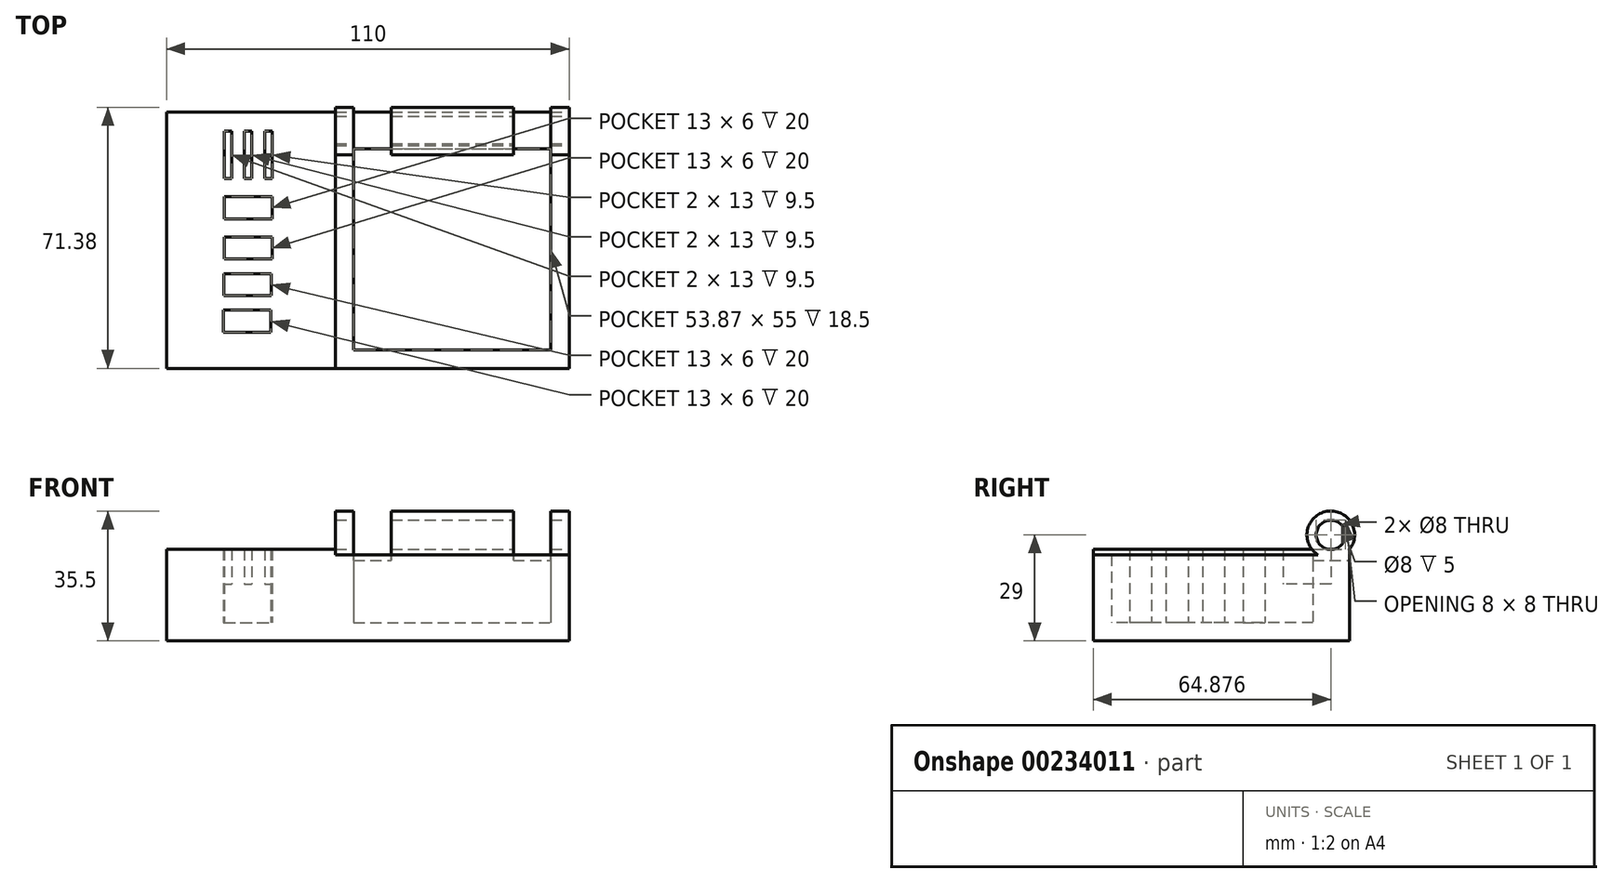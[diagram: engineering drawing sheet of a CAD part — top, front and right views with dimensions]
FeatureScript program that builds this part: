
annotation { "Feature Type Name" : "Feature", "Feature Type Description" : "" }
export const myFeature = defineFeature(function(context is Context, id is Id, definition is map)
    precondition{}
    {
        {
            var Q0;
            Q0=qCreatedBy(makeId("Top.planeOp"),FACE);
            var sketch = newSketch(context, id + "F0", { "sketchPlane" : qUnion([Q0])});
            skLineSegment(sketch, "E0.bottom", {"start": v(0, 0) * mm, "end": v(13, 0) * mm});
            skLineSegment(sketch, "E0.top", {"start": v(0, 6) * mm, "end": v(13, 6) * mm});
            skLineSegment(sketch, "E0.left", {"start": v(0, 0) * mm, "end": v(0, 6) * mm});
            skLineSegment(sketch, "E0.right", {"start": v(13, 0) * mm, "end": v(13, 6) * mm});
            skLineSegment(sketch, "E1.bottom", {"start": v(0, 24) * mm, "end": v(2, 24) * mm});
            skLineSegment(sketch, "E1.top", {"start": v(0, 11) * mm, "end": v(2, 11) * mm});
            skLineSegment(sketch, "E1.left", {"start": v(0, 24) * mm, "end": v(0, 11) * mm});
            skLineSegment(sketch, "E1.right", {"start": v(2, 24) * mm, "end": v(2, 11) * mm});
            skLineSegment(sketch, "E2.bottom", {"start": v(5.5, 24) * mm, "end": v(7.5, 24) * mm});
            skLineSegment(sketch, "E2.top", {"start": v(5.5, 11) * mm, "end": v(7.5, 11) * mm});
            skLineSegment(sketch, "E2.left", {"start": v(5.5, 24) * mm, "end": v(5.5, 11) * mm});
            skLineSegment(sketch, "E2.right", {"start": v(7.5, 24) * mm, "end": v(7.5, 11) * mm});
            skLineSegment(sketch, "E3.bottom", {"start": v(11, 24) * mm, "end": v(13, 24) * mm});
            skLineSegment(sketch, "E3.top", {"start": v(11, 11) * mm, "end": v(13, 11) * mm});
            skLineSegment(sketch, "E3.left", {"start": v(11, 24) * mm, "end": v(11, 11) * mm});
            skLineSegment(sketch, "E3.right", {"start": v(13, 24) * mm, "end": v(13, 11) * mm});
            skLineSegment(sketch, "E4", {"start": v(2, 11) * mm, "end": v(5.5, 11) * mm, "construction": true});
            skLineSegment(sketch, "E5", {"start": v(7.5, 11) * mm, "end": v(11, 11) * mm, "construction": true});
            skLineSegment(sketch, "E6.bottom", {"start": v(0, -5) * mm, "end": v(13, -5) * mm});
            skLineSegment(sketch, "E6.top", {"start": v(0, -11) * mm, "end": v(13, -11) * mm});
            skLineSegment(sketch, "E6.left", {"start": v(0, -5) * mm, "end": v(0, -11) * mm});
            skLineSegment(sketch, "E6.right", {"start": v(13, -5) * mm, "end": v(13, -11) * mm});
            skLineSegment(sketch, "E7.bottom", {"start": v(35.31, 19.1) * mm, "end": v(89.18, 19.1) * mm});
            skLineSegment(sketch, "E7.top", {"start": v(35.32, -35.9) * mm, "end": v(89.19, -35.9) * mm});
            skLineSegment(sketch, "E7.left", {"start": v(35.31, 19.1) * mm, "end": v(35.32, -35.9) * mm});
            skLineSegment(sketch, "E7.right", {"start": v(89.18, 19.1) * mm, "end": v(89.19, -35.9) * mm});
            skLineSegment(sketch, "E8.bottom", {"start": v(-15.81, -40.9) * mm, "end": v(94.19, -40.9) * mm});
            skLineSegment(sketch, "E8.top", {"start": v(-15.82, 29.1) * mm, "end": v(94.19, 29.1) * mm});
            skLineSegment(sketch, "E8.left", {"start": v(-15.81, -40.9) * mm, "end": v(-15.82, 29.1) * mm});
            skLineSegment(sketch, "E8.right", {"start": v(94.19, -40.9) * mm, "end": v(94.19, 29.1) * mm});
            skLineSegment(sketch, "E9.1.0.0", {"start": v(-0.16, -21) * mm, "end": v(12.84, -21) * mm});
            skLineSegment(sketch, "E9.1.0.1", {"start": v(-0.16, -15) * mm, "end": v(-0.16, -21) * mm});
            skLineSegment(sketch, "E9.1.0.2", {"start": v(-0.16, -15) * mm, "end": v(12.84, -15) * mm});
            skLineSegment(sketch, "E9.1.0.3", {"start": v(12.84, -15) * mm, "end": v(12.84, -21) * mm});
            skLineSegment(sketch, "E9.2.0.0", {"start": v(-0.31, -31) * mm, "end": v(12.69, -31) * mm});
            skLineSegment(sketch, "E9.2.0.1", {"start": v(-0.31, -25) * mm, "end": v(-0.31, -31) * mm});
            skLineSegment(sketch, "E9.2.0.2", {"start": v(-0.31, -25) * mm, "end": v(12.69, -25) * mm});
            skLineSegment(sketch, "E9.2.0.3", {"start": v(12.69, -25) * mm, "end": v(12.69, -31) * mm});
            skLineSegment(sketch, "E9.direction1", {"start": v(0, -11) * mm, "end": v(-0.16, -21) * mm, "construction": true});
            skSolve(sketch);
        }
        {
            var Q0;
            Q0=makeQuery(id+"F0.imprint","IMPRINT",FACE,{"disambiguationData":[TD([[makeQuery(id+"F0.imprint","IMPRINT",EDGE,{"derivedFrom":sQuery(id+"F0.wireOp",EDGE,"E0.bottom")}),-1.0]])]});
            extrude(context, id + "F1", {"entities" : qUnion([Q0]), "depth" : 25 * mm});
        }
        {
            var Q0;
            Q0=makeQuery(id+"F1.opExtrude","CAP_FACE",FACE,{"disambiguationData":[OSD([sQuery(id+"F0.wireOp",EDGE,"E0.bottom"),sQuery(id+"F0.wireOp",EDGE,"E0.top"),sQuery(id+"F0.wireOp",EDGE,"E0.left"),sQuery(id+"F0.wireOp",EDGE,"E0.right"),sQuery(id+"F0.wireOp",EDGE,"E1.bottom"),sQuery(id+"F0.wireOp",EDGE,"E1.top"),sQuery(id+"F0.wireOp",EDGE,"E1.left"),sQuery(id+"F0.wireOp",EDGE,"E1.right"),sQuery(id+"F0.wireOp",EDGE,"E2.bottom"),sQuery(id+"F0.wireOp",EDGE,"E2.top"),sQuery(id+"F0.wireOp",EDGE,"E2.left"),sQuery(id+"F0.wireOp",EDGE,"E2.right"),sQuery(id+"F0.wireOp",EDGE,"E3.bottom"),sQuery(id+"F0.wireOp",EDGE,"E3.top"),sQuery(id+"F0.wireOp",EDGE,"E3.left"),sQuery(id+"F0.wireOp",EDGE,"E3.right"),sQuery(id+"F0.wireOp",EDGE,"E6.bottom"),sQuery(id+"F0.wireOp",EDGE,"E6.top"),sQuery(id+"F0.wireOp",EDGE,"E6.left"),sQuery(id+"F0.wireOp",EDGE,"E6.right"),sQuery(id+"F0.wireOp",EDGE,"Jhem5B7e-PwaY-wi88-L2AS-oDyRLYaUdTvM.top"),sQuery(id+"F0.wireOp",EDGE,"Jhem5B7e-PwaY-wi88-L2AS-oDyRLYaUdTvM.right"),sQuery(id+"F0.wireOp",EDGE,"dHCuu3V0-Hv5L-0egd-wwGA-Vg7BnMR16jFB.bottom"),sQuery(id+"F0.wireOp",EDGE,"dHCuu3V0-Hv5L-0egd-wwGA-Vg7BnMR16jFB.top"),sQuery(id+"F0.wireOp",EDGE,"dHCuu3V0-Hv5L-0egd-wwGA-Vg7BnMR16jFB.left"),sQuery(id+"F0.wireOp",EDGE,"dHCuu3V0-Hv5L-0egd-wwGA-Vg7BnMR16jFB.right"),sQuery(id+"F0.wireOp",EDGE,"6ZkocFOk-AnUZ-cton-rGbu-JuxtpcTcdqMe"),sQuery(id+"F0.wireOp",EDGE,"PdukZ5u5-dsJj-gbYv-5oKE-4uIxkKqPsWSn"),sQuery(id+"F0.wireOp",EDGE,"E7.bottom"),sQuery(id+"F0.wireOp",EDGE,"E7.top"),sQuery(id+"F0.wireOp",EDGE,"E7.left"),sQuery(id+"F0.wireOp",EDGE,"E7.right"),sQuery(id+"F0.wireOp",EDGE,"E8.bottom"),sQuery(id+"F0.wireOp",EDGE,"E8.top"),sQuery(id+"F0.wireOp",EDGE,"E8.left"),sQuery(id+"F0.wireOp",EDGE,"E8.right")])],"isStart":true});
            var sketch = newSketch(context, id + "F2", { "sketchPlane" : qUnion([Q0])});
            skLineSegment(sketch, "E10.bottom", {"start": v(89.18, -19.1) * mm, "end": v(35.32, -19.1) * mm});
            skLineSegment(sketch, "E10.top", {"start": v(89.18, 35.9) * mm, "end": v(35.32, 35.9) * mm});
            skLineSegment(sketch, "E10.left", {"start": v(89.18, -19.1) * mm, "end": v(89.18, 35.9) * mm});
            skLineSegment(sketch, "E10.right", {"start": v(35.32, -19.1) * mm, "end": v(35.32, 35.9) * mm});
            skLineSegment(sketch, "E11.bottom", {"start": v(13, -6) * mm, "end": v(0, -6) * mm});
            skLineSegment(sketch, "E11.top", {"start": v(13, 0) * mm, "end": v(0, 0) * mm});
            skLineSegment(sketch, "E11.left", {"start": v(13, -6) * mm, "end": v(13, 0) * mm});
            skLineSegment(sketch, "E11.right", {"start": v(0, -6) * mm, "end": v(0, 0) * mm});
            skLineSegment(sketch, "E12.bottom", {"start": v(13, 5) * mm, "end": v(0, 5) * mm});
            skLineSegment(sketch, "E12.top", {"start": v(13, 11) * mm, "end": v(0, 11) * mm});
            skLineSegment(sketch, "E12.left", {"start": v(13, 5) * mm, "end": v(13, 11) * mm});
            skLineSegment(sketch, "E12.right", {"start": v(0, 5) * mm, "end": v(0, 11) * mm});
            skSolve(sketch);
        }
        {
            var Q0;
            Q0=makeQuery(id+"F2.imprint","IMPRINT",FACE,{"disambiguationData":[TD([[makeQuery(id+"F2.imprint","IMPRINT",EDGE,{"derivedFrom":sQuery(id+"F2.wireOp",EDGE,"E10.bottom")}),1.0]])]});
            var Q1;
            Q1=makeQuery(id+"F2.imprint","IMPRINT",FACE,{"disambiguationData":[TD([[makeQuery(id+"F2.imprint","IMPRINT",EDGE,{"derivedFrom":sQuery(id+"F2.wireOp",EDGE,"E11.bottom")}),1.0]])]});
            var Q2;
            Q2=makeQuery(id+"F2.imprint","IMPRINT",FACE,{"disambiguationData":[TD([[makeQuery(id+"F2.imprint","IMPRINT",EDGE,{"derivedFrom":sQuery(id+"F2.wireOp",EDGE,"E12.bottom")}),1.0]])]});
            var Q3;
            Q3=makeQuery(id+"F2.imprint","IMPRINT",FACE,{"disambiguationData":[TD([[makeQuery(id+"F2.imprint","IMPRINT",EDGE,{"derivedFrom":sQuery(id+"F2.wireOp",EDGE,"BDkRQzdd-od42-jESW-7ooD-0bF7jNIlFtZo.bottom")}),1.0]])]});
            var Q4;
            Q4=makeQuery(id+"F2.imprint","IMPRINT",FACE,{"disambiguationData":[TD([[makeQuery(id+"F2.imprint","IMPRINT",EDGE,{"derivedFrom":sQuery(id+"F2.wireOp",EDGE,"YnWAU6LA-DngU-H7TV-ikAZ-Mie4OEYWa2Z2.bottom")}),1.0]])]});
            extrude(context, id + "F3", {"entities" : qUnion([Q0, Q1, Q2, Q3, Q4]), "operationType" : NewBodyOperationType.ADD, "oppositeDirection" : true, "depth" : 5 * mm});
        }
        {
            var Q0;
            Q0=makeQuery(id+"F3.boolean.opBoolean","MERGE",FACE,{"derivedFrom":[makeQuery(id+"F1.opExtrude","CAP_FACE",FACE,{"disambiguationData":[OSD([sQuery(id+"F0.wireOp",EDGE,"E0.bottom"),sQuery(id+"F0.wireOp",EDGE,"E0.top"),sQuery(id+"F0.wireOp",EDGE,"E0.left"),sQuery(id+"F0.wireOp",EDGE,"E0.right"),sQuery(id+"F0.wireOp",EDGE,"E1.bottom"),sQuery(id+"F0.wireOp",EDGE,"E1.top"),sQuery(id+"F0.wireOp",EDGE,"E1.left"),sQuery(id+"F0.wireOp",EDGE,"E1.right"),sQuery(id+"F0.wireOp",EDGE,"E2.bottom"),sQuery(id+"F0.wireOp",EDGE,"E2.top"),sQuery(id+"F0.wireOp",EDGE,"E2.left"),sQuery(id+"F0.wireOp",EDGE,"E2.right"),sQuery(id+"F0.wireOp",EDGE,"E3.bottom"),sQuery(id+"F0.wireOp",EDGE,"E3.top"),sQuery(id+"F0.wireOp",EDGE,"E3.left"),sQuery(id+"F0.wireOp",EDGE,"E3.right"),sQuery(id+"F0.wireOp",EDGE,"E6.bottom"),sQuery(id+"F0.wireOp",EDGE,"E6.top"),sQuery(id+"F0.wireOp",EDGE,"E6.left"),sQuery(id+"F0.wireOp",EDGE,"E6.right"),sQuery(id+"F0.wireOp",EDGE,"Jhem5B7e-PwaY-wi88-L2AS-oDyRLYaUdTvM.top"),sQuery(id+"F0.wireOp",EDGE,"Jhem5B7e-PwaY-wi88-L2AS-oDyRLYaUdTvM.right"),sQuery(id+"F0.wireOp",EDGE,"dHCuu3V0-Hv5L-0egd-wwGA-Vg7BnMR16jFB.bottom"),sQuery(id+"F0.wireOp",EDGE,"dHCuu3V0-Hv5L-0egd-wwGA-Vg7BnMR16jFB.top"),sQuery(id+"F0.wireOp",EDGE,"dHCuu3V0-Hv5L-0egd-wwGA-Vg7BnMR16jFB.left"),sQuery(id+"F0.wireOp",EDGE,"dHCuu3V0-Hv5L-0egd-wwGA-Vg7BnMR16jFB.right"),sQuery(id+"F0.wireOp",EDGE,"6ZkocFOk-AnUZ-cton-rGbu-JuxtpcTcdqMe"),sQuery(id+"F0.wireOp",EDGE,"PdukZ5u5-dsJj-gbYv-5oKE-4uIxkKqPsWSn"),sQuery(id+"F0.wireOp",EDGE,"E7.bottom"),sQuery(id+"F0.wireOp",EDGE,"E7.top"),sQuery(id+"F0.wireOp",EDGE,"E7.left"),sQuery(id+"F0.wireOp",EDGE,"E7.right"),sQuery(id+"F0.wireOp",EDGE,"E8.bottom"),sQuery(id+"F0.wireOp",EDGE,"E8.top"),sQuery(id+"F0.wireOp",EDGE,"E8.left"),sQuery(id+"F0.wireOp",EDGE,"E8.right")])],"isStart":true}),makeQuery(id+"F3.opExtrude","CAP_FACE",FACE,{"disambiguationData":[OSD([sQuery(id+"F2.wireOp",EDGE,"E10.bottom"),sQuery(id+"F2.wireOp",EDGE,"E10.top"),sQuery(id+"F2.wireOp",EDGE,"E10.left"),sQuery(id+"F2.wireOp",EDGE,"E10.right")])],"isStart":true}),makeQuery(id+"F3.opExtrude","CAP_FACE",FACE,{"disambiguationData":[OSD([sQuery(id+"F2.wireOp",EDGE,"E11.bottom"),sQuery(id+"F2.wireOp",EDGE,"E11.top"),sQuery(id+"F2.wireOp",EDGE,"E11.left"),sQuery(id+"F2.wireOp",EDGE,"E11.right")])],"isStart":true}),makeQuery(id+"F3.opExtrude","CAP_FACE",FACE,{"disambiguationData":[OSD([sQuery(id+"F2.wireOp",EDGE,"E12.bottom"),sQuery(id+"F2.wireOp",EDGE,"E12.top"),sQuery(id+"F2.wireOp",EDGE,"E12.left"),sQuery(id+"F2.wireOp",EDGE,"E12.right")])],"isStart":true}),makeQuery(id+"F3.opExtrude","CAP_FACE",FACE,{"disambiguationData":[OSD([sQuery(id+"F2.wireOp",EDGE,"YnWAU6LA-DngU-H7TV-ikAZ-Mie4OEYWa2Z2.bottom"),sQuery(id+"F2.wireOp",EDGE,"YnWAU6LA-DngU-H7TV-ikAZ-Mie4OEYWa2Z2.top"),sQuery(id+"F2.wireOp",EDGE,"YnWAU6LA-DngU-H7TV-ikAZ-Mie4OEYWa2Z2.left"),sQuery(id+"F2.wireOp",EDGE,"YnWAU6LA-DngU-H7TV-ikAZ-Mie4OEYWa2Z2.right")])],"isStart":true}),makeQuery(id+"F3.opExtrude","CAP_FACE",FACE,{"disambiguationData":[OSD([sQuery(id+"F2.wireOp",EDGE,"BDkRQzdd-od42-jESW-7ooD-0bF7jNIlFtZo.bottom"),sQuery(id+"F2.wireOp",EDGE,"BDkRQzdd-od42-jESW-7ooD-0bF7jNIlFtZo.top"),sQuery(id+"F2.wireOp",EDGE,"BDkRQzdd-od42-jESW-7ooD-0bF7jNIlFtZo.left"),sQuery(id+"F2.wireOp",EDGE,"BDkRQzdd-od42-jESW-7ooD-0bF7jNIlFtZo.right")])],"isStart":true})]});
            var sketch = newSketch(context, id + "F4", { "sketchPlane" : qUnion([Q0])});
            skLineSegment(sketch, "E13.bottom", {"start": v(13, -24) * mm, "end": v(11, -24) * mm});
            skLineSegment(sketch, "E13.top", {"start": v(13, -11) * mm, "end": v(11, -11) * mm});
            skLineSegment(sketch, "E13.left", {"start": v(13, -24) * mm, "end": v(13, -11) * mm});
            skLineSegment(sketch, "E13.right", {"start": v(11, -24) * mm, "end": v(11, -11) * mm});
            skLineSegment(sketch, "E14.bottom", {"start": v(7.5, -11) * mm, "end": v(5.5, -11) * mm});
            skLineSegment(sketch, "E14.top", {"start": v(7.5, -24) * mm, "end": v(5.5, -24) * mm});
            skLineSegment(sketch, "E14.left", {"start": v(7.5, -11) * mm, "end": v(7.5, -24) * mm});
            skLineSegment(sketch, "E14.right", {"start": v(5.5, -11) * mm, "end": v(5.5, -24) * mm});
            skLineSegment(sketch, "E15.bottom", {"start": v(2, -24) * mm, "end": v(0, -24) * mm});
            skLineSegment(sketch, "E15.top", {"start": v(2, -11) * mm, "end": v(0, -11) * mm});
            skLineSegment(sketch, "E15.left", {"start": v(2, -24) * mm, "end": v(2, -11) * mm});
            skLineSegment(sketch, "E15.right", {"start": v(0, -24) * mm, "end": v(0, -11) * mm});
            skSolve(sketch);
        }
        {
            var Q0;
            Q0=makeQuery(id+"F4.imprint","IMPRINT",FACE,{"disambiguationData":[TD([[makeQuery(id+"F4.imprint","IMPRINT",EDGE,{"derivedFrom":sQuery(id+"F4.wireOp",EDGE,"E13.bottom")}),1.0]])]});
            var Q1;
            Q1=makeQuery(id+"F4.imprint","IMPRINT",FACE,{"disambiguationData":[TD([[makeQuery(id+"F4.imprint","IMPRINT",EDGE,{"derivedFrom":sQuery(id+"F4.wireOp",EDGE,"E14.bottom")}),-1.0]])]});
            var Q2;
            Q2=makeQuery(id+"F4.imprint","IMPRINT",FACE,{"disambiguationData":[TD([[makeQuery(id+"F4.imprint","IMPRINT",EDGE,{"derivedFrom":sQuery(id+"F4.wireOp",EDGE,"E15.bottom")}),1.0]])]});
            extrude(context, id + "F5", {"entities" : qUnion([Q0, Q1, Q2]), "operationType" : NewBodyOperationType.ADD, "oppositeDirection" : true, "depth" : (25 - 9.5) * mm});
        }
        {
            var Q0;
            Q0=makeQuery(id+"F1.opExtrude","SWEPT_FACE",FACE,{"disambiguationData":[OSD([sQuery(id+"F0.wireOp",EDGE,"E8.right")])]});
            var sketch = newSketch(context, id + "F6", { "sketchPlane" : qUnion([Q0])});
            skCircle(sketch, "E16", {"center": v(23.98, 29) * mm, "radius": 4 * mm});
            skCircle(sketch, "E17", {"center": v(23.98, 29) * mm, "radius": 6.5 * mm});
            skSolve(sketch);
        }
        {
            var Q0;
            Q0 = qSketchRegion(id + "F6", true);
            extrude(context, id + "F7", {"entities" : qUnion([Q0]), "operationType" : NewBodyOperationType.ADD, "oppositeDirection" : true, "depth" : (53.87 + 10) * mm});
        }
        {
            var Q0;
            Q0=makeQuery(id+"F1.opExtrude","CAP_FACE",FACE,{"disambiguationData":[OSD([sQuery(id+"F0.wireOp",EDGE,"E0.bottom"),sQuery(id+"F0.wireOp",EDGE,"E0.top"),sQuery(id+"F0.wireOp",EDGE,"E0.left"),sQuery(id+"F0.wireOp",EDGE,"E0.right"),sQuery(id+"F0.wireOp",EDGE,"E1.bottom"),sQuery(id+"F0.wireOp",EDGE,"E1.top"),sQuery(id+"F0.wireOp",EDGE,"E1.left"),sQuery(id+"F0.wireOp",EDGE,"E1.right"),sQuery(id+"F0.wireOp",EDGE,"E2.bottom"),sQuery(id+"F0.wireOp",EDGE,"E2.top"),sQuery(id+"F0.wireOp",EDGE,"E2.left"),sQuery(id+"F0.wireOp",EDGE,"E2.right"),sQuery(id+"F0.wireOp",EDGE,"E3.bottom"),sQuery(id+"F0.wireOp",EDGE,"E3.top"),sQuery(id+"F0.wireOp",EDGE,"E3.left"),sQuery(id+"F0.wireOp",EDGE,"E3.right"),sQuery(id+"F0.wireOp",EDGE,"E6.bottom"),sQuery(id+"F0.wireOp",EDGE,"E6.top"),sQuery(id+"F0.wireOp",EDGE,"E6.left"),sQuery(id+"F0.wireOp",EDGE,"E6.right"),sQuery(id+"F0.wireOp",EDGE,"Jhem5B7e-PwaY-wi88-L2AS-oDyRLYaUdTvM.top"),sQuery(id+"F0.wireOp",EDGE,"Jhem5B7e-PwaY-wi88-L2AS-oDyRLYaUdTvM.right"),sQuery(id+"F0.wireOp",EDGE,"dHCuu3V0-Hv5L-0egd-wwGA-Vg7BnMR16jFB.bottom"),sQuery(id+"F0.wireOp",EDGE,"dHCuu3V0-Hv5L-0egd-wwGA-Vg7BnMR16jFB.top"),sQuery(id+"F0.wireOp",EDGE,"dHCuu3V0-Hv5L-0egd-wwGA-Vg7BnMR16jFB.left"),sQuery(id+"F0.wireOp",EDGE,"dHCuu3V0-Hv5L-0egd-wwGA-Vg7BnMR16jFB.right"),sQuery(id+"F0.wireOp",EDGE,"6ZkocFOk-AnUZ-cton-rGbu-JuxtpcTcdqMe"),sQuery(id+"F0.wireOp",EDGE,"PdukZ5u5-dsJj-gbYv-5oKE-4uIxkKqPsWSn"),sQuery(id+"F0.wireOp",EDGE,"E7.bottom"),sQuery(id+"F0.wireOp",EDGE,"E7.top"),sQuery(id+"F0.wireOp",EDGE,"E7.left"),sQuery(id+"F0.wireOp",EDGE,"E7.right"),sQuery(id+"F0.wireOp",EDGE,"E8.bottom"),sQuery(id+"F0.wireOp",EDGE,"E8.top"),sQuery(id+"F0.wireOp",EDGE,"E8.left"),sQuery(id+"F0.wireOp",EDGE,"E8.right")])],"isStart":false});
            var sketch = newSketch(context, id + "F8", { "sketchPlane" : qUnion([Q0])});
            skLineSegment(sketch, "E18.bottom", {"start": v(35.31, 18.85) * mm, "end": v(45.56, 18.85) * mm});
            skLineSegment(sketch, "E18.top", {"start": v(35.31, 29.1) * mm, "end": v(45.56, 29.1) * mm});
            skLineSegment(sketch, "E18.left", {"start": v(35.31, 18.85) * mm, "end": v(35.31, 29.1) * mm});
            skLineSegment(sketch, "E18.right", {"start": v(45.56, 18.85) * mm, "end": v(45.56, 29.1) * mm});
            skLineSegment(sketch, "E19.bottom", {"start": v(89.19, 18.85) * mm, "end": v(78.94, 18.85) * mm});
            skLineSegment(sketch, "E19.top", {"start": v(89.19, 29.1) * mm, "end": v(78.94, 29.1) * mm});
            skLineSegment(sketch, "E19.left", {"start": v(89.19, 18.85) * mm, "end": v(89.19, 29.1) * mm});
            skLineSegment(sketch, "E19.right", {"start": v(78.94, 18.85) * mm, "end": v(78.94, 29.1) * mm});
            skLineSegment(sketch, "E20.top", {"start": v(35.31, 34.1) * mm, "end": v(45.56, 34.1) * mm});
            skLineSegment(sketch, "E20.left", {"start": v(35.31, 29.1) * mm, "end": v(35.31, 34.1) * mm});
            skLineSegment(sketch, "E20.right", {"start": v(45.56, 29.1) * mm, "end": v(45.56, 34.1) * mm});
            skLineSegment(sketch, "E21.top", {"start": v(35.31, 13.85) * mm, "end": v(45.56, 13.85) * mm});
            skLineSegment(sketch, "E21.left", {"start": v(35.31, 18.85) * mm, "end": v(35.31, 13.85) * mm});
            skLineSegment(sketch, "E21.right", {"start": v(45.56, 18.85) * mm, "end": v(45.56, 13.85) * mm});
            skLineSegment(sketch, "E22.bottom", {"start": v(78.94, 29.1) * mm, "end": v(89.19, 29.1) * mm});
            skLineSegment(sketch, "E22.top", {"start": v(78.94, 34.1) * mm, "end": v(89.19, 34.1) * mm});
            skLineSegment(sketch, "E22.left", {"start": v(78.94, 29.1) * mm, "end": v(78.94, 34.1) * mm});
            skLineSegment(sketch, "E22.right", {"start": v(89.19, 29.1) * mm, "end": v(89.19, 34.1) * mm});
            skLineSegment(sketch, "E23.top", {"start": v(89.19, 13.85) * mm, "end": v(78.94, 13.85) * mm});
            skLineSegment(sketch, "E23.left", {"start": v(89.19, 18.85) * mm, "end": v(89.19, 13.85) * mm});
            skLineSegment(sketch, "E23.right", {"start": v(78.94, 18.85) * mm, "end": v(78.94, 13.85) * mm});
            skSolve(sketch);
        }
        {
            var Q0;
            Q0 = qSketchRegion(id + "F8", true);
            extrude(context, id + "F9", {"entities" : qUnion([Q0]), "operationType" : NewBodyOperationType.REMOVE, "depth" : 25 * mm});
        }
        {
            var Q0;
            Q0=makeQuery(id+"F7.boolean.opBoolean","MERGE",FACE,{"derivedFrom":[makeQuery(id+"F1.opExtrude","SWEPT_FACE",FACE,{"disambiguationData":[OSD([sQuery(id+"F0.wireOp",EDGE,"E8.right")])]}),makeQuery(id+"F7.opExtrude","CAP_FACE",FACE,{"disambiguationData":[OSD([sQuery(id+"F6.wireOp",EDGE,"E16"),sQuery(id+"F6.wireOp",EDGE,"E17")])],"isStart":true})]});
            var sketch = newSketch(context, id + "F10", { "sketchPlane" : qUnion([Q0])});
            skCircle(sketch, "E24", {"center": v(23.98, 29) * mm, "radius": 6.5 * mm});
            skLineSegment(sketch, "E25", {"start": v(23.98, 29) * mm, "end": v(23.98, 22.5) * mm});
            skLineSegment(sketch, "E26", {"start": v(23.98, 22.5) * mm, "end": v(-40.9, 22.5) * mm});
            skLineSegment(sketch, "E27", {"start": v(-40.9, 22.5) * mm, "end": v(-40.9, 25) * mm});
            skLineSegment(sketch, "E28", {"start": v(-40.9, 25) * mm, "end": v(18.85, 25) * mm});
            skSolve(sketch);
        }
        {
            var Q0;
            {var subQ2=sQuery(id+"F10.wireOp",EDGE,"E26");Q0=makeQuery(id+"F10.imprint","IMPRINT",FACE,{"disambiguationData":[TD([[makeQuery(id+"F10.imprint","IMPRINT",EDGE,{"derivedFrom":subQ2}),-1.0]])]});}
            var Q1;
            Q1=makeQuery(id+"F7.opExtrude","CAP_FACE",FACE,{"disambiguationData":[OSD([sQuery(id+"F6.wireOp",EDGE,"E16"),sQuery(id+"F6.wireOp",EDGE,"E17")])],"isStart":false});
            extrude(context, id + "F11", {"entities" : qUnion([Q0]), "operationType" : NewBodyOperationType.REMOVE, "endBound" : BoundingType.UP_TO_SURFACE, "oppositeDirection" : true, "endBoundEntityFace" : qUnion([Q1]), "depth" : 25 * mm});
        }
        {
            var Q0;
            Q0=makeQuery(id+"F11.boolean.opBoolean","COPY",FACE,{"derivedFrom":makeQuery(id+"F11.opExtrude","SWEPT_FACE",FACE,{"disambiguationData":[OSD([sQuery(id+"F10.wireOp",EDGE,"E26")])]})});
            var sketch = newSketch(context, id + "F12", { "sketchPlane" : qUnion([Q0])});
            skLineSegment(sketch, "E29.0", {"start": v(30.31, -40.9) * mm, "end": v(30.31, 23.98) * mm});
            skLineSegment(sketch, "E29.1", {"start": v(35.31, 19.1) * mm, "end": v(35.32, -35.9) * mm});
            skLineSegment(sketch, "E29.2", {"start": v(30.31, -40.9) * mm, "end": v(94.18, -40.9) * mm});
            skLineSegment(sketch, "E29.3", {"start": v(35.32, -35.9) * mm, "end": v(89.19, -35.9) * mm});
            skLineSegment(sketch, "E29.4", {"start": v(89.18, 19.1) * mm, "end": v(89.19, -35.9) * mm});
            skLineSegment(sketch, "E29.5", {"start": v(94.19, 23.98) * mm, "end": v(94.19, -40.9) * mm});
            skLineSegment(sketch, "E29.6", {"start": v(30.31, 23.98) * mm, "end": v(94.18, 23.98) * mm});
            skSolve(sketch);
        }
        {
            var Q0;
            Q0=makeQuery(id+"F12.imprint","IMPRINT",FACE,{"disambiguationData":[TD([[makeQuery(id+"F12.imprint","IMPRINT",EDGE,{"derivedFrom":sQuery(id+"F12.wireOp",EDGE,"E29.0")}),-1.0]])]});
            extrude(context, id + "F13", {"entities" : qUnion([Q0]), "operationType" : NewBodyOperationType.ADD, "depth" : 1 * mm});
        }
        {
            var Q0;
            Q0=makeQuery(id+"F9.boolean.opBoolean","COPY",FACE,{"derivedFrom":makeQuery(id+"F9.opExtrude","CAP_FACE",FACE,{"disambiguationData":[OSD([sQuery(id+"F8.wireOp",EDGE,"E18.left"),sQuery(id+"F8.wireOp",EDGE,"E18.right"),sQuery(id+"F8.wireOp",EDGE,"E20.top"),sQuery(id+"F8.wireOp",EDGE,"E20.left"),sQuery(id+"F8.wireOp",EDGE,"E20.right"),sQuery(id+"F8.wireOp",EDGE,"E21.top"),sQuery(id+"F8.wireOp",EDGE,"E21.left"),sQuery(id+"F8.wireOp",EDGE,"E21.right")])],"isStart":true})});
            var sketch = newSketch(context, id + "F14", { "sketchPlane" : qUnion([Q0])});
            skLineSegment(sketch, "E30.bottom", {"start": v(35.31, 29.1) * mm, "end": v(45.56, 29.1) * mm});
            skLineSegment(sketch, "E30.top", {"start": v(35.31, 18.85) * mm, "end": v(45.56, 18.85) * mm});
            skLineSegment(sketch, "E30.left", {"start": v(35.31, 29.1) * mm, "end": v(35.31, 18.85) * mm});
            skLineSegment(sketch, "E30.right", {"start": v(45.56, 29.1) * mm, "end": v(45.56, 18.85) * mm});
            skSolve(sketch);
        }
        {
            var Q0;
            Q0 = qSketchRegion(id + "F14", true);
            extrude(context, id + "F15", {"entities" : qUnion([Q0]), "operationType" : NewBodyOperationType.REMOVE, "oppositeDirection" : true, "depth" : 3 * mm});
        }
        {
            var Q0;
            Q0=makeQuery(id+"F9.boolean.opBoolean","COPY",FACE,{"derivedFrom":makeQuery(id+"F9.opExtrude","CAP_FACE",FACE,{"disambiguationData":[OSD([sQuery(id+"F8.wireOp",EDGE,"E19.left"),sQuery(id+"F8.wireOp",EDGE,"E19.right"),sQuery(id+"F8.wireOp",EDGE,"E22.top"),sQuery(id+"F8.wireOp",EDGE,"E22.left"),sQuery(id+"F8.wireOp",EDGE,"E22.right"),sQuery(id+"F8.wireOp",EDGE,"E23.top"),sQuery(id+"F8.wireOp",EDGE,"E23.left"),sQuery(id+"F8.wireOp",EDGE,"E23.right")])],"isStart":true})});
            extrude(context, id + "F16", {"entities" : qUnion([Q0]), "operationType" : NewBodyOperationType.REMOVE, "oppositeDirection" : true, "depth" : 3 * mm});
        }
        {
            var Q0;
            {var subQ0=sQuery(id+"F0.wireOp",EDGE,"E9.2.0.2");var subQ1=sQuery(id+"F0.wireOp",EDGE,"E9.2.0.0");var subQ2=sQuery(id+"F0.wireOp",EDGE,"E9.1.0.3");var subQ3=sQuery(id+"F0.wireOp",EDGE,"E9.1.0.2");var subQ4=sQuery(id+"F0.wireOp",EDGE,"E9.1.0.1");var subQ5=sQuery(id+"F0.wireOp",EDGE,"E9.1.0.0");var subQ6=sQuery(id+"F0.wireOp",EDGE,"E8.right");var subQ7=sQuery(id+"F0.wireOp",EDGE,"E8.left");var subQ8=sQuery(id+"F0.wireOp",EDGE,"E8.top");var subQ9=sQuery(id+"F0.wireOp",EDGE,"E8.bottom");var subQ10=sQuery(id+"F0.wireOp",EDGE,"E3.right");var subQ11=sQuery(id+"F0.wireOp",EDGE,"E3.left");var subQ12=sQuery(id+"F0.wireOp",EDGE,"E3.top");var subQ13=sQuery(id+"F0.wireOp",EDGE,"E3.bottom");var subQ14=sQuery(id+"F0.wireOp",EDGE,"E2.right");var subQ15=sQuery(id+"F0.wireOp",EDGE,"E2.left");var subQ16=sQuery(id+"F0.wireOp",EDGE,"E2.top");var subQ17=sQuery(id+"F0.wireOp",EDGE,"E2.bottom");var subQ18=sQuery(id+"F0.wireOp",EDGE,"E1.right");var subQ19=sQuery(id+"F0.wireOp",EDGE,"E1.left");var subQ20=sQuery(id+"F0.wireOp",EDGE,"E1.top");var subQ21=sQuery(id+"F0.wireOp",EDGE,"E1.bottom");Q0=makeQuery(id+"F5.boolean.opBoolean","MERGE",FACE,{"derivedFrom":[makeQuery(id+"F3.boolean.opBoolean","MERGE",FACE,{"derivedFrom":[makeQuery(id+"F1.opExtrude","CAP_FACE",FACE,{"disambiguationData":[OSD([sQuery(id+"F0.wireOp",EDGE,"E0.bottom"),sQuery(id+"F0.wireOp",EDGE,"E0.top"),sQuery(id+"F0.wireOp",EDGE,"E0.left"),sQuery(id+"F0.wireOp",EDGE,"E0.right"),subQ21,subQ20,subQ19,subQ18,subQ17,subQ16,subQ15,subQ14,subQ13,subQ12,subQ11,subQ10,sQuery(id+"F0.wireOp",EDGE,"E6.bottom"),sQuery(id+"F0.wireOp",EDGE,"E6.top"),sQuery(id+"F0.wireOp",EDGE,"E6.left"),sQuery(id+"F0.wireOp",EDGE,"E6.right"),sQuery(id+"F0.wireOp",EDGE,"E7.bottom"),sQuery(id+"F0.wireOp",EDGE,"E7.top"),sQuery(id+"F0.wireOp",EDGE,"E7.left"),sQuery(id+"F0.wireOp",EDGE,"E7.right"),subQ9,subQ8,subQ7,subQ6,subQ5,subQ4,subQ3,subQ2,subQ1,sQuery(id+"F0.wireOp",EDGE,"E9.2.0.1"),subQ0,sQuery(id+"F0.wireOp",EDGE,"E9.2.0.3")])],"isStart":true}),makeQuery(id+"F3.opExtrude","CAP_FACE",FACE,{"disambiguationData":[OSD([subQ21,subQ20,subQ19,subQ18,subQ17,subQ16,subQ15,subQ14,subQ13,subQ12,subQ11,subQ10,subQ9,subQ8,subQ7,subQ6,subQ5,subQ4,subQ3,subQ2,subQ1,subQ0,sQuery(id+"F2.wireOp",EDGE,"YnWAU6LA-DngU-H7TV-ikAZ-Mie4OEYWa2Z2.bottom"),sQuery(id+"F2.wireOp",EDGE,"YnWAU6LA-DngU-H7TV-ikAZ-Mie4OEYWa2Z2.top"),sQuery(id+"F2.wireOp",EDGE,"YnWAU6LA-DngU-H7TV-ikAZ-Mie4OEYWa2Z2.left"),sQuery(id+"F2.wireOp",EDGE,"YnWAU6LA-DngU-H7TV-ikAZ-Mie4OEYWa2Z2.right"),sQuery(id+"F2.wireOp",EDGE,"BDkRQzdd-od42-jESW-7ooD-0bF7jNIlFtZo.bottom"),sQuery(id+"F2.wireOp",EDGE,"BDkRQzdd-od42-jESW-7ooD-0bF7jNIlFtZo.top"),sQuery(id+"F2.wireOp",EDGE,"BDkRQzdd-od42-jESW-7ooD-0bF7jNIlFtZo.left"),sQuery(id+"F2.wireOp",EDGE,"BDkRQzdd-od42-jESW-7ooD-0bF7jNIlFtZo.right")])],"isStart":true})]}),makeQuery(id+"F5.opExtrude","CAP_FACE",FACE,{"disambiguationData":[OSD([sQuery(id+"F4.wireOp",EDGE,"E13.bottom"),sQuery(id+"F4.wireOp",EDGE,"E13.top"),sQuery(id+"F4.wireOp",EDGE,"E13.left"),sQuery(id+"F4.wireOp",EDGE,"E13.right")])],"isStart":true}),makeQuery(id+"F5.opExtrude","CAP_FACE",FACE,{"disambiguationData":[OSD([sQuery(id+"F4.wireOp",EDGE,"E14.bottom"),sQuery(id+"F4.wireOp",EDGE,"E14.top"),sQuery(id+"F4.wireOp",EDGE,"E14.left"),sQuery(id+"F4.wireOp",EDGE,"E14.right")])],"isStart":true}),makeQuery(id+"F5.opExtrude","CAP_FACE",FACE,{"disambiguationData":[OSD([sQuery(id+"F4.wireOp",EDGE,"E15.bottom"),sQuery(id+"F4.wireOp",EDGE,"E15.top"),sQuery(id+"F4.wireOp",EDGE,"E15.left"),sQuery(id+"F4.wireOp",EDGE,"E15.right")])],"isStart":true})]});}
            var sketch = newSketch(context, id + "F17", { "sketchPlane" : qUnion([Q0])});
            skLineSegment(sketch, "E31.bottom", {"start": v(12.84, 15) * mm, "end": v(-0.16, 15) * mm});
            skLineSegment(sketch, "E31.top", {"start": v(12.84, 21) * mm, "end": v(-0.16, 21) * mm});
            skLineSegment(sketch, "E31.left", {"start": v(12.84, 15) * mm, "end": v(12.84, 21) * mm});
            skLineSegment(sketch, "E31.right", {"start": v(-0.16, 15) * mm, "end": v(-0.16, 21) * mm});
            skLineSegment(sketch, "E32.bottom", {"start": v(12.69, 25) * mm, "end": v(-0.31, 25) * mm});
            skLineSegment(sketch, "E32.top", {"start": v(12.69, 31) * mm, "end": v(-0.31, 31) * mm});
            skLineSegment(sketch, "E32.left", {"start": v(12.69, 25) * mm, "end": v(12.69, 31) * mm});
            skLineSegment(sketch, "E32.right", {"start": v(-0.31, 25) * mm, "end": v(-0.31, 31) * mm});
            skSolve(sketch);
        }
        {
            var Q0;
            Q0 = qSketchRegion(id + "F17", true);
            extrude(context, id + "F18", {"entities" : qUnion([Q0]), "operationType" : NewBodyOperationType.ADD, "oppositeDirection" : true, "depth" : 5 * mm});
        }
    });
